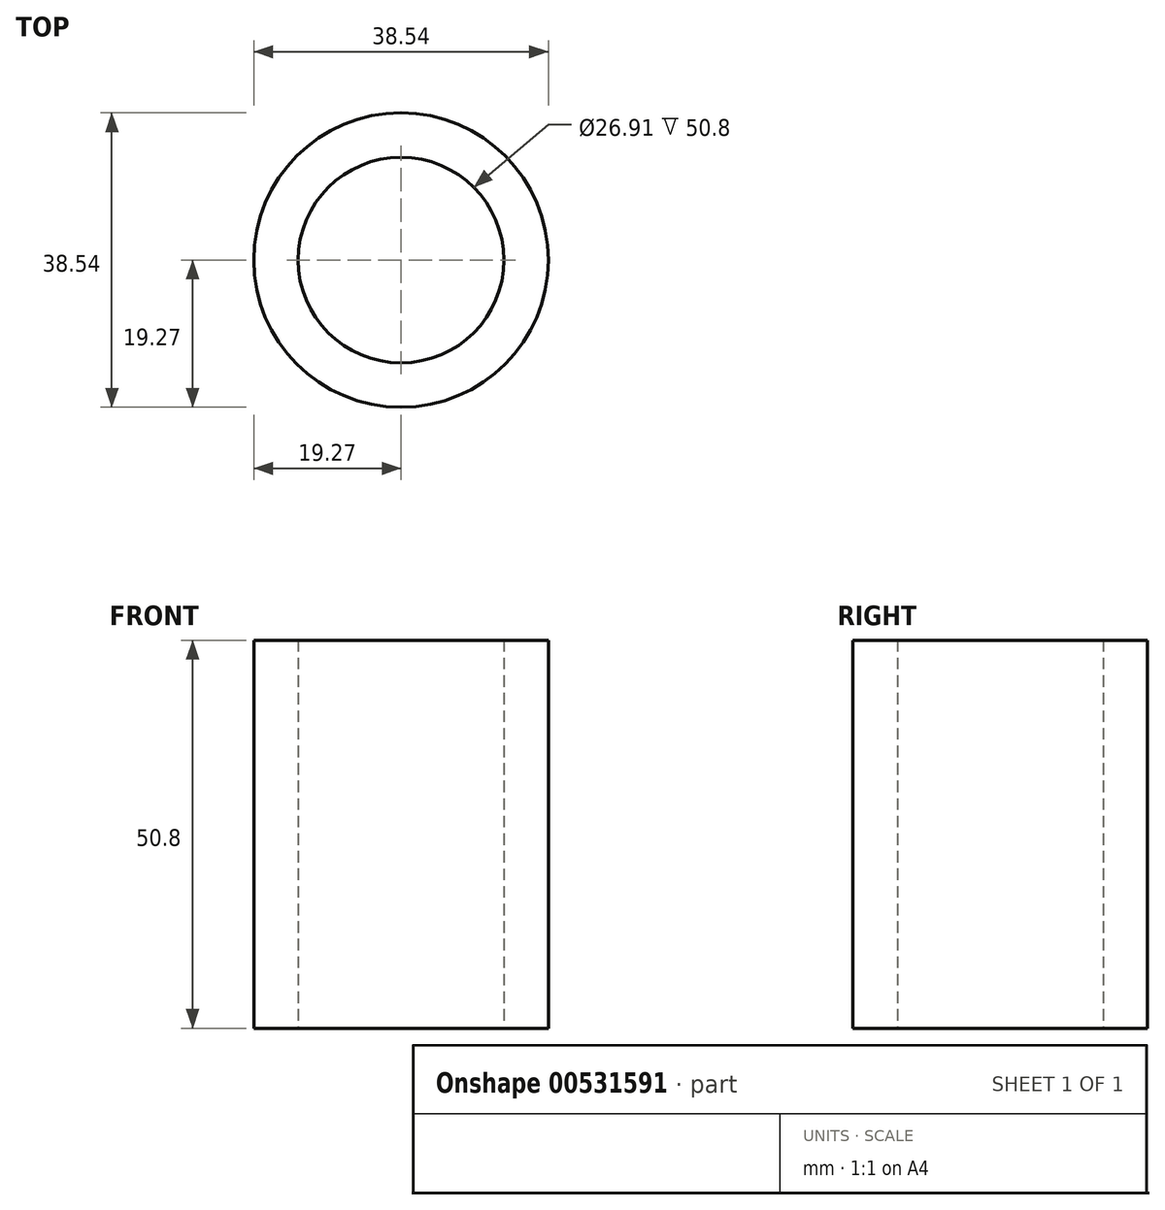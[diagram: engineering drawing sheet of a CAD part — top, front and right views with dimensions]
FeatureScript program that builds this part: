
annotation { "Feature Type Name" : "Feature", "Feature Type Description" : "" }
export const myFeature = defineFeature(function(context is Context, id is Id, definition is map)
    precondition{}
    {
        {
            var Q0;
            Q0=qCreatedBy(makeId("Top.planeOp"),FACE);
            var sketch = newSketch(context, id + "F0", { "sketchPlane" : qUnion([Q0])});
            skCircle(sketch, "E0", {"center": v(0, 0) * mm, "radius": 19.27 * mm});
            skSolve(sketch);
        }
        {
            var Q0;
            Q0 = qSketchRegion(id + "F0", true);
            extrude(context, id + "F1", {"entities" : qUnion([Q0]), "depth" : 50.8 * mm, "offsetDistance" : 25.4 * mm});
        }
        {
            var Q0;
            Q0=qCreatedBy(makeId("Top.planeOp"),FACE);
            var sketch = newSketch(context, id + "F2", { "sketchPlane" : qUnion([Q0])});
            skCircle(sketch, "E1", {"center": v(0, 0) * mm, "radius": 13.45 * mm});
            skSolve(sketch);
        }
        {
            var Q0;
            Q0 = qSketchRegion(id + "F2", true);
            extrude(context, id + "F3", {"entities" : qUnion([Q0]), "operationType" : NewBodyOperationType.REMOVE, "depth" : 54.6 * mm, "offsetDistance" : 25.4 * mm});
        }
    });
